# Revit family: TopVent_THC
name_source: partatom
category: Mechanical Equipment
revit_build: Autodesk Revit MEP 2015 (Build: 20160512_0715(x64)
units: mm (PartAtom-declared; Revit-internal decimal feet)

## types (9) — shared parameters
COBIE Connected load = 3.6 kW
COBIE Current consumption max. = 5.9A
COBIE Extract air temperature max. = 50°C
COBIE Frequency = 50 Hz
COBIE Permitted voltage tolerance = +/-5%
COBIE Pressure of the heating medium max. = 800 kPa
COBIE Protection rating = IP 54
COBIE Series fuse = 13A
COBIE Static efficiency of the fans = 63.6%
COBIE Supply air temperature max. = 60°C
COBIE Supply voltage = 3x400 V AC
COBIE Temperature of the heating medium max. = 90°C
Connected load = 3.6 kW
Current consumption max. = 5.9A
Extract air temperature max. = 50°C
Frequency = 50 Hz
Permitted voltage tolerance = +/-5%
Pressure of the heating medium max. = 800 kPa
Protection rating = IP 54
S = 25 mm  [stored 0.082021 ft]
Series fuse = 13A
Static efficiency of the fans = 63.6%
Supply air temperature max. = 60°C
Supply voltage = 3x400 V AC
Temperature of the heating medium max. = 90°C

## per-type parameters (varying)
- THC-6-AC: (X)=1120 mm  [stored 3.67454 ft]; A=900 mm  [stored 2.95276 ft]; Air flow rate=3100 m3/h; B=1647 mm  [stored 5.40354 ft]; COBIE Air flow rate=3100 m3/h; COBIE Condensate quantity=90 kg/h; COBIE Condensate quantity 22 °C (50/70 %) - 6/12 °C=0.0/13.5 kg/h; COBIE Condensate quantity 22 °C (50/70 %) - 8/14 °C=0.0/7.9 kg/h; COBIE Condensate quantity 26 °C (50/70 %) - 6/12 °C=8.6/30.2 kg/h; COBIE Condensate quantity 26 °C (50/70 %) - 8/14 °C=3.0/24.6 kg/h; COBIE Effective electric power input=0.72 kW; COBIE Floor area covered=537.0; COBIE Heat output 16/20 °C (60/40 °C)=18.8/16.2 kW; COBIE Heat output 16/20 °C (80/60 °C)=32.8/30.3 kW; COBIE Maximum mounting height 16/20 °C (60/40 °C)=16.8/17.9 m; COBIE Maximum mounting height 16/20 °C (80/60 °C)=13.4/14.0 m; COBIE Nominal air flow rate=6000.0; COBIE Octave sound power level - 1000 Hz=71 dB; COBIE Octave sound power level - 125 Hz=59 dB; COBIE Octave sound power level - 2000 Hz=71 dB; COBIE Octave sound power level - 250 Hz=62 dB; COBIE Octave sound power level - 4000 Hz=67 dB; COBIE Octave sound power level - 500 Hz=68 dB; COBIE Octave sound power level - 63 Hz=41 dB; COBIE Octave sound power level - 8000 Hz=58 dB; COBIE Sensible cooling capacity 22 °C (50/70 %) - 6/12 °C=20.4/18.5 kW; COBIE Sensible cooling capacity 22 °C (50/70 %) - 8/14 °C=20.4/16.0 kW; COBIE Sensible cooling capacity 26 °C (50/70 %) - 6/12 °C=25.2/23.2 kW; COBIE Sensible cooling capacity 26 °C (50/70 %) - 8/14 °C=22.7/20.8 kW; COBIE Sound pressure level (at a distance of 5 m)=54 dB(A); COBIE Supply air temperature 16/20 °C (60/40 °C)=27.3/30.0 °C; COBIE Supply air temperature 16/20 °C (80/60 °C)=34.2/37.0 °C; COBIE Supply air temperature 22 °C (50/70 %) - 6/12 °C=13.9/14.9 °C; COBIE Supply air temperature 22 °C (50/70 %) - 8/14 °C=13.9/16.1 °C; COBIE Supply air temperature 26 °C (50/70 %) - 6/12 °C=15.5/16.5 °C; COBIE Supply air temperature 26 °C (50/70 %) - 8/14 °C=16.7/17.7 °C; COBIE Total cooling capacity 22 °C (50/70 %) - 6/12 °C=20.4/27.7 kW; COBIE Total cooling capacity 22 °C (50/70 %) - 8/14 °C=20.4/21.4 kW; COBIE Total cooling capacity 26 °C (50/70 %) - 6/12 °C=31.1/43.7 kW; COBIE Total cooling capacity 26 °C (50/70 %) - 8/14 °C=24.8/37.5 kW; COBIE Total sound power level=76 dB(A); COBIE Water content of cooling coil=7.9 l; COBIE Water content of heating coil=4.6 l; COBIE Water pressure drop 16/20 °C (60/40 °C)=2/2 kPa; COBIE Water pressure drop 16/20 °C (80/60 °C)=7/6 kPa; COBIE Water pressure drop 22 °C (50/70 %) - 6/12 °C=15/28 kPa; COBIE Water pressure drop 22 °C (50/70 %) - 8/14 °C=15/17 kPa; COBIE Water pressure drop 26 °C (50/70 %) - 6/12 °C=36/71 kPa; COBIE Water pressure drop 26 °C (50/70 %) - 8/14 °C=23/52 kPa; COBIE Water quantity 16/20 °C (60/40 °C)=807/697 l/h; COBIE Water quantity 16/20 °C (80/60 °C)=1410/1301 l/h; COBIE Water quantity 22 °C (50/70 %) - 6/12 °C=2925/3960 l/h; COBIE Water quantity 22 °C (50/70 %) - 8/14 °C=2925/3064 l/h; COBIE Water quantity 26 °C (50/70 %) - 6/12 °C=4448/6263 l/h; COBIE Water quantity 26 °C (50/70 %) - 8/14 °C=3552/5367 l/h; COBIE Weight=248 kg; Condensate quantity=90 kg/h; Condensate quantity 22 °C (50/70 %) - 6/12 °C=0.0/13.5 kg/h; Condensate quantity 22 °C (50/70 %) - 8/14 °C=0.0/7.9 kg/h; Condensate quantity 26 °C (50/70 %) - 6/12 °C=8.6/30.2 kg/h; Condensate quantity 26 °C (50/70 %) - 8/14 °C=3.0/24.6 kg/h; E=594 mm  [stored 1.94882 ft]; E/2=297 mm  [stored 0.974409 ft]; Effective electric power input=0.72 kW; F=758 mm  [stored 2.48688 ft]; Floor area covered=537 m²; G=101 mm  [stored 0.331365 ft]; H=179 mm  [stored 0.58727 ft]; Heat output 16/20 °C (60/40 °C)=18.8/16.2 kW; Heat output 16/20 °C (80/60 °C)=32.8/30.3 kW; I=349 mm  [stored 1.14501 ft]; J=427 mm  [stored 1.40092 ft]; K=760 mm  [stored 2.49344 ft]; Maximum mounting height 16/20 °C (60/40 °C)=16.8/17.9 m; Maximum mounting height 16/20 °C (80/60 °C)=13.4/14.0 m; N=1030 mm  [stored 3.37927 ft]; Nominal air flow rate=6000 m³/h; O=792 mm  [stored 2.59843 ft]; Octave sound power level - 1000 Hz=71 dB; Octave sound power level - 125 Hz=59 dB; Octave sound power level - 2000 Hz=71 dB; Octave sound power level - 250 Hz=62 dB; Octave sound power level - 4000 Hz=67 dB; Octave sound power level - 500 Hz=68 dB; Octave sound power level - 63 Hz=41 dB; Octave sound power level - 8000 Hz=58 dB; P=312 mm  [stored 1.02362 ft]; Q=32 mm  [stored 0.104987 ft]; R=32 mm  [stored 0.104987 ft]; Sensible cooling capacity 22 °C (50/70 %) - 6/12 °C=20.4/18.5 kW; Sensible cooling capacity 22 °C (50/70 %) - 8/14 °C=20.4/16.0 kW; Sensible cooling capacity 26 °C (50/70 %) - 6/12 °C=25.2/23.2 kW; Sensible cooling capacity 26 °C (50/70 %) - 8/14 °C=22.7/20.8 kW; Sound pressure level (at a distance of 5 m)=54 dB(A); Supply air temperature 16/20 °C (60/40 °C)=27.3/30.0 °C; Supply air temperature 16/20 °C (80/60 °C)=34.2/37.0 °C; Supply air temperature 22 °C (50/70 %) - 6/12 °C=13.9/14.9 °C; Supply air temperature 22 °C (50/70 %) - 8/14 °C=13.9/16.1 °C; Supply air temperature 26 °C (50/70 %) - 6/12 °C=15.5/16.5 °C; Supply air temperature 26 °C (50/70 %) - 8/14 °C=16.7/17.7 °C; Total cooling capacity 22 °C (50/70 %) - 6/12 °C=20.4/27.7 kW; Total cooling capacity 22 °C (50/70 %) - 8/14 °C=20.4/21.4 kW; Total cooling capacity 26 °C (50/70 %) - 6/12 °C=31.1/43.7 kW; Total cooling capacity 26 °C (50/70 %) - 8/14 °C=24.8/37.5 kW; Total sound power level=76 dB(A); Water content of cooling coil=7.9 l; Water content of heating coil=4.6 l; Water pressure drop 16/20 °C (60/40 °C)=2/2 kPa; Water pressure drop 16/20 °C (80/60 °C)=7/6 kPa; Water pressure drop 22 °C (50/70 %) - 6/12 °C=15/28 kPa; Water pressure drop 22 °C (50/70 %) - 8/14 °C=15/17 kPa; Water pressure drop 26 °C (50/70 %) - 6/12 °C=36/71 kPa; Water pressure drop 26 °C (50/70 %) - 8/14 °C=23/52 kPa; Water quantity 16/20 °C (60/40 °C)=807/697 l/h; Water quantity 16/20 °C (80/60 °C)=1410/1301 l/h; Water quantity 22 °C (50/70 %) - 6/12 °C=2925/3960 l/h; Water quantity 22 °C (50/70 %) - 8/14 °C=2925/3064 l/h; Water quantity 26 °C (50/70 %) - 6/12 °C=4448/6263 l/h; Water quantity 26 °C (50/70 %) - 8/14 °C=3552/5367 l/h; Weight=248 kg
- THC-6-BC: (X)=1120 mm  [stored 3.67454 ft]; A=900 mm  [stored 2.95276 ft]; Air flow rate=3100 m3/h; B=1647 mm  [stored 5.40354 ft]; COBIE Air flow rate=3100 m3/h; COBIE Condensate quantity=90 kg/h; COBIE Condensate quantity 22 °C (50/70 %) - 6/12 °C=0.0/13.5 kg/h; COBIE Condensate quantity 22 °C (50/70 %) - 8/14 °C=0.0/7.9 kg/h; COBIE Condensate quantity 26 °C (50/70 %) - 6/12 °C=8.6/30.2 kg/h; COBIE Condensate quantity 26 °C (50/70 %) - 8/14 °C=3.0/24.6 kg/h; COBIE Effective electric power input=0.76 kW; COBIE Floor area covered=537.0; COBIE Heat output 16/20 °C (60/40 °C)=26.9/23.3 kW; COBIE Heat output 16/20 °C (80/60 °C)=47.0/43.4 kW; COBIE Maximum mounting height 16/20 °C (60/40 °C)=14.6/15.5 m; COBIE Maximum mounting height 16/20 °C (80/60 °C)=11.6/12.0 m; COBIE Nominal air flow rate=6000.0; COBIE Octave sound power level - 1000 Hz=71 dB; COBIE Octave sound power level - 125 Hz=59 dB; COBIE Octave sound power level - 2000 Hz=71 dB; COBIE Octave sound power level - 250 Hz=62 dB; COBIE Octave sound power level - 4000 Hz=67 dB; COBIE Octave sound power level - 500 Hz=68 dB; COBIE Octave sound power level - 63 Hz=41 dB; COBIE Octave sound power level - 8000 Hz=58 dB; COBIE Sensible cooling capacity 22 °C (50/70 %) - 6/12 °C=20.4/18.5 kW; COBIE Sensible cooling capacity 22 °C (50/70 %) - 8/14 °C=20.4/16.0 kW; COBIE Sensible cooling capacity 26 °C (50/70 %) - 6/12 °C=25.2/23.2 kW; COBIE Sensible cooling capacity 26 °C (50/70 %) - 8/14 °C=22.7/20.8 kW; COBIE Sound pressure level (at a distance of 5 m)=54 dB(A); COBIE Supply air temperature 16/20 °C (60/40 °C)=31.3/33.5 °C; COBIE Supply air temperature 16/20 °C (80/60 °C)=41.3/43.5 °C; COBIE Supply air temperature 22 °C (50/70 %) - 6/12 °C=13.9/14.9 °C; COBIE Supply air temperature 22 °C (50/70 %) - 8/14 °C=13.9/16.1 °C; COBIE Supply air temperature 26 °C (50/70 %) - 6/12 °C=15.5/16.5 °C; COBIE Supply air temperature 26 °C (50/70 %) - 8/14 °C=16.7/17.7 °C; COBIE Total cooling capacity 22 °C (50/70 %) - 6/12 °C=20.4/27.7 kW; COBIE Total cooling capacity 22 °C (50/70 %) - 8/14 °C=20.4/21.4 kW; COBIE Total cooling capacity 26 °C (50/70 %) - 6/12 °C=31.1/43.7 kW; COBIE Total cooling capacity 26 °C (50/70 %) - 8/14 °C=24.8/37.5 kW; COBIE Total sound power level=76 dB(A); COBIE Water content of cooling coil=7.9 l; COBIE Water content of heating coil=4.6 l; COBIE Water pressure drop 16/20 °C (60/40 °C)=4/3 kPa; COBIE Water pressure drop 16/20 °C (80/60 °C)=13/11 kPa; COBIE Water pressure drop 22 °C (50/70 %) - 6/12 °C=15/28 kPa; COBIE Water pressure drop 22 °C (50/70 %) - 8/14 °C=15/17 kPa; COBIE Water pressure drop 26 °C (50/70 %) - 6/12 °C=36/71 kPa; COBIE Water pressure drop 26 °C (50/70 %) - 8/14 °C=23/52 kPa; COBIE Water quantity 16/20 °C (60/40 °C)=1157/1001 l/h; COBIE Water quantity 16/20 °C (80/60 °C)=2020/1864 l/h; COBIE Water quantity 22 °C (50/70 %) - 6/12 °C=2925/3960 l/h; COBIE Water quantity 22 °C (50/70 %) - 8/14 °C=2925/3064 l/h; COBIE Water quantity 26 °C (50/70 %) - 6/12 °C=4448/6263 l/h; COBIE Water quantity 26 °C (50/70 %) - 8/14 °C=3552/5367 l/h; COBIE Weight=248 kg; Condensate quantity=90 kg/h; Condensate quantity 22 °C (50/70 %) - 6/12 °C=0.0/13.5 kg/h; Condensate quantity 22 °C (50/70 %) - 8/14 °C=0.0/7.9 kg/h; Condensate quantity 26 °C (50/70 %) - 6/12 °C=8.6/30.2 kg/h; Condensate quantity 26 °C (50/70 %) - 8/14 °C=3.0/24.6 kg/h; E=594 mm  [stored 1.94882 ft]; E/2=297 mm  [stored 0.974409 ft]; Effective electric power input=0.76 kW; F=758 mm  [stored 2.48688 ft]; Floor area covered=537 m²; G=101 mm  [stored 0.331365 ft]; H=179 mm  [stored 0.58727 ft]; Heat output 16/20 °C (60/40 °C)=26.9/23.3 kW; Heat output 16/20 °C (80/60 °C)=47.0/43.4 kW; I=349 mm  [stored 1.14501 ft]; J=427 mm  [stored 1.40092 ft]; K=760 mm  [stored 2.49344 ft]; Maximum mounting height 16/20 °C (60/40 °C)=14.6/15.5 m; Maximum mounting height 16/20 °C (80/60 °C)=11.6/12.0 m; N=1030 mm  [stored 3.37927 ft]; Nominal air flow rate=6000 m³/h; O=792 mm  [stored 2.59843 ft]; Octave sound power level - 1000 Hz=71 dB; Octave sound power level - 125 Hz=59 dB; Octave sound power level - 2000 Hz=71 dB; Octave sound power level - 250 Hz=62 dB; Octave sound power level - 4000 Hz=67 dB; Octave sound power level - 500 Hz=68 dB; Octave sound power level - 63 Hz=41 dB; Octave sound power level - 8000 Hz=58 dB; P=312 mm  [stored 1.02362 ft]; Q=32 mm  [stored 0.104987 ft]; R=32 mm  [stored 0.104987 ft]; Sensible cooling capacity 22 °C (50/70 %) - 6/12 °C=20.4/18.5 kW; Sensible cooling capacity 22 °C (50/70 %) - 8/14 °C=20.4/16.0 kW; Sensible cooling capacity 26 °C (50/70 %) - 6/12 °C=25.2/23.2 kW; Sensible cooling capacity 26 °C (50/70 %) - 8/14 °C=22.7/20.8 kW; Sound pressure level (at a distance of 5 m)=54 dB(A); Supply air temperature 16/20 °C (60/40 °C)=31.3/33.5 °C; Supply air temperature 16/20 °C (80/60 °C)=41.3/43.5 °C; Supply air temperature 22 °C (50/70 %) - 6/12 °C=13.9/14.9 °C; Supply air temperature 22 °C (50/70 %) - 8/14 °C=13.9/16.1 °C; Supply air temperature 26 °C (50/70 %) - 6/12 °C=15.5/16.5 °C; Supply air temperature 26 °C (50/70 %) - 8/14 °C=16.7/17.7 °C; Total cooling capacity 22 °C (50/70 %) - 6/12 °C=20.4/27.7 kW; Total cooling capacity 22 °C (50/70 %) - 8/14 °C=20.4/21.4 kW; Total cooling capacity 26 °C (50/70 %) - 6/12 °C=31.1/43.7 kW; Total cooling capacity 26 °C (50/70 %) - 8/14 °C=24.8/37.5 kW; Total sound power level=76 dB(A); Water content of cooling coil=7.9 l; Water content of heating coil=4.6 l; Water pressure drop 16/20 °C (60/40 °C)=4/3 kPa; Water pressure drop 16/20 °C (80/60 °C)=13/11 kPa; Water pressure drop 22 °C (50/70 %) - 6/12 °C=15/28 kPa; Water pressure drop 22 °C (50/70 %) - 8/14 °C=15/17 kPa; Water pressure drop 26 °C (50/70 %) - 6/12 °C=36/71 kPa; Water pressure drop 26 °C (50/70 %) - 8/14 °C=23/52 kPa; Water quantity 16/20 °C (60/40 °C)=1157/1001 l/h; Water quantity 16/20 °C (80/60 °C)=2020/1864 l/h; Water quantity 22 °C (50/70 %) - 6/12 °C=2925/3960 l/h; Water quantity 22 °C (50/70 %) - 8/14 °C=2925/3064 l/h; Water quantity 26 °C (50/70 %) - 6/12 °C=4448/6263 l/h; Water quantity 26 °C (50/70 %) - 8/14 °C=3552/5367 l/h; Weight=248 kg
- THC-6-CC: (X)=1120 mm  [stored 3.67454 ft]; A=900 mm  [stored 2.95276 ft]; Air flow rate=3100 m3/h; B=1647 mm  [stored 5.40354 ft]; COBIE Air flow rate=3100 m3/h; COBIE Condensate quantity=90 kg/h; COBIE Condensate quantity 22 °C (50/70 %) - 6/12 °C=0.0/13.5 kg/h; COBIE Condensate quantity 22 °C (50/70 %) - 8/14 °C=0.0/7.9 kg/h; COBIE Condensate quantity 26 °C (50/70 %) - 6/12 °C=8.6/30.2 kg/h; COBIE Condensate quantity 26 °C (50/70 %) - 8/14 °C=3.0/24.6 kg/h; COBIE Effective electric power input=0.87 kW; COBIE Floor area covered=537.0; COBIE Heat output 16/20 °C (60/40 °C)=45.0/39.3 kW; COBIE Heat output 16/20 °C (80/60 °C)=76.0/70.3 kW; COBIE Maximum mounting height 16/20 °C (60/40 °C)=11.8/12.5 m; COBIE Maximum mounting height 16/20 °C (80/60 °C)=9.4/9.8 m; COBIE Nominal air flow rate=6000.0; COBIE Octave sound power level - 1000 Hz=71 dB; COBIE Octave sound power level - 125 Hz=59 dB; COBIE Octave sound power level - 2000 Hz=71 dB; COBIE Octave sound power level - 250 Hz=62 dB; COBIE Octave sound power level - 4000 Hz=67 dB; COBIE Octave sound power level - 500 Hz=68 dB; COBIE Octave sound power level - 63 Hz=41 dB; COBIE Octave sound power level - 8000 Hz=58 dB; COBIE Sensible cooling capacity 22 °C (50/70 %) - 6/12 °C=20.4/18.5 kW; COBIE Sensible cooling capacity 22 °C (50/70 %) - 8/14 °C=20.4/16.0 kW; COBIE Sensible cooling capacity 26 °C (50/70 %) - 6/12 °C=25.2/23.2 kW; COBIE Sensible cooling capacity 26 °C (50/70 %) - 8/14 °C=22.7/20.8 kW; COBIE Sound pressure level (at a distance of 5 m)=54 dB(A); COBIE Supply air temperature 16/20 °C (60/40 °C)=40.3/41.5 °C; COBIE Supply air temperature 16/20 °C (80/60 °C)=55.6/56.8 °C; COBIE Supply air temperature 22 °C (50/70 %) - 6/12 °C=13.9/14.9 °C; COBIE Supply air temperature 22 °C (50/70 %) - 8/14 °C=13.9/16.1 °C; COBIE Supply air temperature 26 °C (50/70 %) - 6/12 °C=15.5/16.5 °C; COBIE Supply air temperature 26 °C (50/70 %) - 8/14 °C=16.7/17.7 °C; COBIE Total cooling capacity 22 °C (50/70 %) - 6/12 °C=20.4/27.7 kW; COBIE Total cooling capacity 22 °C (50/70 %) - 8/14 °C=20.4/21.4 kW; COBIE Total cooling capacity 26 °C (50/70 %) - 6/12 °C=31.1/43.7 kW; COBIE Total cooling capacity 26 °C (50/70 %) - 8/14 °C=24.8/37.5 kW; COBIE Total sound power level=76 dB(A); COBIE Water content of cooling coil=7.9 l; COBIE Water content of heating coil=7.9 l; COBIE Water pressure drop 16/20 °C (60/40 °C)=6/5 kPa; COBIE Water pressure drop 16/20 °C (80/60 °C)=18/16 kPa; COBIE Water pressure drop 22 °C (50/70 %) - 6/12 °C=15/28 kPa; COBIE Water pressure drop 22 °C (50/70 %) - 8/14 °C=15/17 kPa; COBIE Water pressure drop 26 °C (50/70 %) - 6/12 °C=36/71 kPa; COBIE Water pressure drop 26 °C (50/70 %) - 8/14 °C=23/52 kPa; COBIE Water quantity 16/20 °C (60/40 °C)=1935/1690 l/h; COBIE Water quantity 16/20 °C (80/60 °C)=3267/3022 l/h; COBIE Water quantity 22 °C (50/70 %) - 6/12 °C=2925/3960 l/h; COBIE Water quantity 22 °C (50/70 %) - 8/14 °C=2925/3064 l/h; COBIE Water quantity 26 °C (50/70 %) - 6/12 °C=4448/6263 l/h; COBIE Water quantity 26 °C (50/70 %) - 8/14 °C=3552/5367 l/h; COBIE Weight=255 kg; Condensate quantity=90 kg/h; Condensate quantity 22 °C (50/70 %) - 6/12 °C=0.0/13.5 kg/h; Condensate quantity 22 °C (50/70 %) - 8/14 °C=0.0/7.9 kg/h; Condensate quantity 26 °C (50/70 %) - 6/12 °C=8.6/30.2 kg/h; Condensate quantity 26 °C (50/70 %) - 8/14 °C=3.0/24.6 kg/h; E=594 mm  [stored 1.94882 ft]; E/2=297 mm  [stored 0.974409 ft]; Effective electric power input=0.87 kW; F=758 mm  [stored 2.48688 ft]; Floor area covered=537 m²; G=101 mm  [stored 0.331365 ft]; H=179 mm  [stored 0.58727 ft]; Heat output 16/20 °C (60/40 °C)=45.0/39.3 kW; Heat output 16/20 °C (80/60 °C)=76.0/70.3 kW; I=349 mm  [stored 1.14501 ft]; J=427 mm  [stored 1.40092 ft]; K=760 mm  [stored 2.49344 ft]; Maximum mounting height 16/20 °C (60/40 °C)=11.8/12.5 m; Maximum mounting height 16/20 °C (80/60 °C)=9.4/9.8 m; N=1030 mm  [stored 3.37927 ft]; Nominal air flow rate=6000 m³/h; O=792 mm  [stored 2.59843 ft]; Octave sound power level - 1000 Hz=71 dB; Octave sound power level - 125 Hz=59 dB; Octave sound power level - 2000 Hz=71 dB; Octave sound power level - 250 Hz=62 dB; Octave sound power level - 4000 Hz=67 dB; Octave sound power level - 500 Hz=68 dB; Octave sound power level - 63 Hz=41 dB; Octave sound power level - 8000 Hz=58 dB; P=312 mm  [stored 1.02362 ft]; Q=32 mm  [stored 0.104987 ft]; R=32 mm  [stored 0.104987 ft]; Sensible cooling capacity 22 °C (50/70 %) - 6/12 °C=20.4/18.5 kW; Sensible cooling capacity 22 °C (50/70 %) - 8/14 °C=20.4/16.0 kW; Sensible cooling capacity 26 °C (50/70 %) - 6/12 °C=25.2/23.2 kW; Sensible cooling capacity 26 °C (50/70 %) - 8/14 °C=22.7/20.8 kW; Sound pressure level (at a distance of 5 m)=54 dB(A); Supply air temperature 16/20 °C (60/40 °C)=40.3/41.5 °C; Supply air temperature 16/20 °C (80/60 °C)=55.6/56.8 °C; Supply air temperature 22 °C (50/70 %) - 6/12 °C=13.9/14.9 °C; Supply air temperature 22 °C (50/70 %) - 8/14 °C=13.9/16.1 °C; Supply air temperature 26 °C (50/70 %) - 6/12 °C=15.5/16.5 °C; Supply air temperature 26 °C (50/70 %) - 8/14 °C=16.7/17.7 °C; Total cooling capacity 22 °C (50/70 %) - 6/12 °C=20.4/27.7 kW; Total cooling capacity 22 °C (50/70 %) - 8/14 °C=20.4/21.4 kW; Total cooling capacity 26 °C (50/70 %) - 6/12 °C=31.1/43.7 kW; Total cooling capacity 26 °C (50/70 %) - 8/14 °C=24.8/37.5 kW; Total sound power level=76 dB(A); Water content of cooling coil=7.9 l; Water content of heating coil=7.9 l; Water pressure drop 16/20 °C (60/40 °C)=6/5 kPa; Water pressure drop 16/20 °C (80/60 °C)=18/16 kPa; Water pressure drop 22 °C (50/70 %) - 6/12 °C=15/28 kPa; Water pressure drop 22 °C (50/70 %) - 8/14 °C=15/17 kPa; Water pressure drop 26 °C (50/70 %) - 6/12 °C=36/71 kPa; Water pressure drop 26 °C (50/70 %) - 8/14 °C=23/52 kPa; Water quantity 16/20 °C (60/40 °C)=1935/1690 l/h; Water quantity 16/20 °C (80/60 °C)=3267/3022 l/h; Water quantity 22 °C (50/70 %) - 6/12 °C=2925/3960 l/h; Water quantity 22 °C (50/70 %) - 8/14 °C=2925/3064 l/h; Water quantity 26 °C (50/70 %) - 6/12 °C=4448/6263 l/h; Water quantity 26 °C (50/70 %) - 8/14 °C=3552/5367 l/h; Weight=255 kg
- THC-9-AC: (X)=1238 mm  [stored 4.06168 ft]; A=1100 mm; Air flow rate=5000 m3/h; B=1765 mm  [stored 5.79068 ft]; COBIE Air flow rate=5000 m3/h; COBIE Condensate quantity=150 kg/h; COBIE Condensate quantity 22 °C (50/70 %) - 6/12 °C=0.0/23.9 kg/h; COBIE Condensate quantity 22 °C (50/70 %) - 8/14 °C=0.0/5.2 kg/h; COBIE Condensate quantity 26 °C (50/70 %) - 6/12 °C=16.3/49.8 kg/h; COBIE Condensate quantity 26 °C (50/70 %) - 8/14 °C=0.0/31.1 kg/h; COBIE Effective electric power input=1.37 kW; COBIE Floor area covered=946.0; COBIE Heat output 16/20 °C (60/40 °C)=31.7/27.4 kW; COBIE Heat output 16/20 °C (80/60 °C)=55.5/51.2 kW; COBIE Maximum mounting height 16/20 °C (60/40 °C)=17.0/18.1 m; COBIE Maximum mounting height 16/20 °C (80/60 °C)=13.6/14.1 m; COBIE Nominal air flow rate=9000.0; COBIE Octave sound power level - 1000 Hz=77 dB; COBIE Octave sound power level - 125 Hz=66 dB; COBIE Octave sound power level - 2000 Hz=76 dB; COBIE Octave sound power level - 250 Hz=69 dB; COBIE Octave sound power level - 4000 Hz=74 dB; COBIE Octave sound power level - 500 Hz=74 dB; COBIE Octave sound power level - 63 Hz=47 dB; COBIE Octave sound power level - 8000 Hz=67 dB; COBIE Sensible cooling capacity 22 °C (50/70 %) - 6/12 °C=31.4/28.4 kW; COBIE Sensible cooling capacity 22 °C (50/70 %) - 8/14 °C=31.4/24.6 kW; COBIE Sensible cooling capacity 26 °C (50/70 %) - 6/12 °C=38.8/35.9 kW; COBIE Sensible cooling capacity 26 °C (50/70 %) - 8/14 °C=35.0/32.0 kW; COBIE Sound pressure level (at a distance of 5 m)=60 dB(A); COBIE Supply air temperature 16/20 °C (60/40 °C)=28.5/31.1 °C; COBIE Supply air temperature 16/20 °C (80/60 °C)=36.3/38.9 °C; COBIE Supply air temperature 22 °C (50/70 %) - 6/12 °C=13.6/14.6 °C; COBIE Supply air temperature 22 °C (50/70 %) - 8/14 °C=13.6/15.9 °C; COBIE Supply air temperature 26 °C (50/70 %) - 6/12 °C=15.2/16.2 °C; COBIE Supply air temperature 26 °C (50/70 %) - 8/14 °C=16.4/17.4 °C; COBIE Total cooling capacity 22 °C (50/70 %) - 6/12 °C=31.4/44.7 kW; COBIE Total cooling capacity 22 °C (50/70 %) - 8/14 °C=31.4/28.2 kW; COBIE Total cooling capacity 26 °C (50/70 %) - 6/12 °C=49.9/69.8 kW; COBIE Total cooling capacity 26 °C (50/70 %) - 8/14 °C=35.0/53.2 kW; COBIE Total sound power level=82 dB(A); COBIE Water content of cooling coil=12.4 l; COBIE Water content of heating coil=7.4 l; COBIE Water pressure drop 16/20 °C (60/40 °C)=3/2 kPa; COBIE Water pressure drop 16/20 °C (80/60 °C)=8/7 kPa; COBIE Water pressure drop 22 °C (50/70 %) - 6/12 °C=15/31 kPa; COBIE Water pressure drop 22 °C (50/70 %) - 8/14 °C=15/12 kPa; COBIE Water pressure drop 26 °C (50/70 %) - 6/12 °C=38/75 kPa; COBIE Water pressure drop 26 °C (50/70 %) - 8/14 °C=19/44 kPa; COBIE Water quantity 16/20 °C (60/40 °C)=1364/1179 l/h; COBIE Water quantity 16/20 °C (80/60 °C)=2386/2201 l/h; COBIE Water quantity 22 °C (50/70 %) - 6/12 °C=4496/6401 l/h; COBIE Water quantity 22 °C (50/70 %) - 8/14 °C=4496/4031 l/h; COBIE Water quantity 26 °C (50/70 %) - 6/12 °C=7149/9989 l/h; COBIE Water quantity 26 °C (50/70 %) - 8/14 °C=5013/7619 l/h; COBIE Weight=318 kg; Condensate quantity=150 kg/h; Condensate quantity 22 °C (50/70 %) - 6/12 °C=0.0/23.9 kg/h; Condensate quantity 22 °C (50/70 %) - 8/14 °C=0.0/5.2 kg/h; Condensate quantity 26 °C (50/70 %) - 6/12 °C=16.3/49.8 kg/h; Condensate quantity 26 °C (50/70 %) - 8/14 °C=0.0/31.1 kg/h; E=846 mm  [stored 2.77559 ft]; E/2=423 mm  [stored 1.3878 ft]; Effective electric power input=1.37 kW; F=882 mm  [stored 2.8937 ft]; Floor area covered=946 m²; G=111 mm; H=189 mm  [stored 0.620079 ft]; Heat output 16/20 °C (60/40 °C)=31.7/27.4 kW; Heat output 16/20 °C (80/60 °C)=55.5/51.2 kW; I=395 mm  [stored 1.29593 ft]; J=473 mm  [stored 1.55184 ft]; K=935 mm; Maximum mounting height 16/20 °C (60/40 °C)=17.0/18.1 m; Maximum mounting height 16/20 °C (80/60 °C)=13.6/14.1 m; N=1230 mm  [stored 4.03543 ft]; Nominal air flow rate=9000 m³/h; O=860 mm; Octave sound power level - 1000 Hz=77 dB; Octave sound power level - 125 Hz=66 dB; Octave sound power level - 2000 Hz=76 dB; Octave sound power level - 250 Hz=69 dB; Octave sound power level - 4000 Hz=74 dB; Octave sound power level - 500 Hz=74 dB; Octave sound power level - 63 Hz=47 dB; Octave sound power level - 8000 Hz=67 dB; P=342 mm  [stored 1.12205 ft]; Q=38 mm; R=38 mm; Sensible cooling capacity 22 °C (50/70 %) - 6/12 °C=31.4/28.4 kW; Sensible cooling capacity 22 °C (50/70 %) - 8/14 °C=31.4/24.6 kW; Sensible cooling capacity 26 °C (50/70 %) - 6/12 °C=38.8/35.9 kW; Sensible cooling capacity 26 °C (50/70 %) - 8/14 °C=35.0/32.0 kW; Sound pressure level (at a distance of 5 m)=60 dB(A); Supply air temperature 16/20 °C (60/40 °C)=28.5/31.1 °C; Supply air temperature 16/20 °C (80/60 °C)=36.3/38.9 °C; Supply air temperature 22 °C (50/70 %) - 6/12 °C=13.6/14.6 °C; Supply air temperature 22 °C (50/70 %) - 8/14 °C=13.6/15.9 °C; Supply air temperature 26 °C (50/70 %) - 6/12 °C=15.2/16.2 °C; Supply air temperature 26 °C (50/70 %) - 8/14 °C=16.4/17.4 °C; Total cooling capacity 22 °C (50/70 %) - 6/12 °C=31.4/44.7 kW; Total cooling capacity 22 °C (50/70 %) - 8/14 °C=31.4/28.2 kW; Total cooling capacity 26 °C (50/70 %) - 6/12 °C=49.9/69.8 kW; Total cooling capacity 26 °C (50/70 %) - 8/14 °C=35.0/53.2 kW; Total sound power level=82 dB(A); Water content of cooling coil=12.4 l; Water content of heating coil=7.4 l; Water pressure drop 16/20 °C (60/40 °C)=3/2 kPa; Water pressure drop 16/20 °C (80/60 °C)=8/7 kPa; Water pressure drop 22 °C (50/70 %) - 6/12 °C=15/31 kPa; Water pressure drop 22 °C (50/70 %) - 8/14 °C=15/12 kPa; Water pressure drop 26 °C (50/70 %) - 6/12 °C=38/75 kPa; Water pressure drop 26 °C (50/70 %) - 8/14 °C=19/44 kPa; Water quantity 16/20 °C (60/40 °C)=1364/1179 l/h; Water quantity 16/20 °C (80/60 °C)=2386/2201 l/h; Water quantity 22 °C (50/70 %) - 6/12 °C=4496/6401 l/h; Water quantity 22 °C (50/70 %) - 8/14 °C=4496/4031 l/h; Water quantity 26 °C (50/70 %) - 6/12 °C=7149/9989 l/h; Water quantity 26 °C (50/70 %) - 8/14 °C=5013/7619 l/h; Weight=318 kg
- THC-9-BC: (X)=1238 mm  [stored 4.06168 ft]; A=1100 mm; Air flow rate=5000 m3/h; B=1765 mm  [stored 5.79068 ft]; COBIE Air flow rate=5000 m3/h; COBIE Condensate quantity=150 kg/h; COBIE Condensate quantity 22 °C (50/70 %) - 6/12 °C=0.0/23.9 kg/h; COBIE Condensate quantity 22 °C (50/70 %) - 8/14 °C=0.0/5.2 kg/h; COBIE Condensate quantity 26 °C (50/70 %) - 6/12 °C=16.3/49.8 kg/h; COBIE Condensate quantity 26 °C (50/70 %) - 8/14 °C=0.0/31.1 kg/h; COBIE Effective electric power input=1.49 kW; COBIE Floor area covered=946.0; COBIE Heat output 16/20 °C (60/40 °C)=40.6/35.1 kW; COBIE Heat output 16/20 °C (80/60 °C)=71.2/65.7 kW; COBIE Maximum mounting height 16/20 °C (60/40 °C)=15.4/16.5 m; COBIE Maximum mounting height 16/20 °C (80/60 °C)=12.2/12.7 m; COBIE Nominal air flow rate=9000.0; COBIE Octave sound power level - 1000 Hz=77 dB; COBIE Octave sound power level - 125 Hz=66 dB; COBIE Octave sound power level - 2000 Hz=76 dB; COBIE Octave sound power level - 250 Hz=69 dB; COBIE Octave sound power level - 4000 Hz=74 dB; COBIE Octave sound power level - 500 Hz=74 dB; COBIE Octave sound power level - 63 Hz=47 dB; COBIE Octave sound power level - 8000 Hz=67 dB; COBIE Sensible cooling capacity 22 °C (50/70 %) - 6/12 °C=31.4/28.4 kW; COBIE Sensible cooling capacity 22 °C (50/70 %) - 8/14 °C=31.4/24.6 kW; COBIE Sensible cooling capacity 26 °C (50/70 %) - 6/12 °C=38.8/35.9 kW; COBIE Sensible cooling capacity 26 °C (50/70 %) - 8/14 °C=35.0/32.0 kW; COBIE Sound pressure level (at a distance of 5 m)=60 dB(A); COBIE Supply air temperature 16/20 °C (60/40 °C)=31.4/33.6 °C; COBIE Supply air temperature 16/20 °C (80/60 °C)=41.5/43.7 °C; COBIE Supply air temperature 22 °C (50/70 %) - 6/12 °C=13.6/14.6 °C; COBIE Supply air temperature 22 °C (50/70 %) - 8/14 °C=13.6/15.9 °C; COBIE Supply air temperature 26 °C (50/70 %) - 6/12 °C=15.2/16.2 °C; COBIE Supply air temperature 26 °C (50/70 %) - 8/14 °C=16.4/17.4 °C; COBIE Total cooling capacity 22 °C (50/70 %) - 6/12 °C=31.4/44.7 kW; COBIE Total cooling capacity 22 °C (50/70 %) - 8/14 °C=31.4/28.2 kW; COBIE Total cooling capacity 26 °C (50/70 %) - 6/12 °C=49.9/69.8 kW; COBIE Total cooling capacity 26 °C (50/70 %) - 8/14 °C=35.0/53.2 kW; COBIE Total sound power level=82 dB(A); COBIE Water content of cooling coil=12.4 l; COBIE Water content of heating coil=7.4 l; COBIE Water pressure drop 16/20 °C (60/40 °C)=4/3 kPa; COBIE Water pressure drop 16/20 °C (80/60 °C)=12/10 kPa; COBIE Water pressure drop 22 °C (50/70 %) - 6/12 °C=15/31 kPa; COBIE Water pressure drop 22 °C (50/70 %) - 8/14 °C=15/12 kPa; COBIE Water pressure drop 26 °C (50/70 %) - 6/12 °C=38/75 kPa; COBIE Water pressure drop 26 °C (50/70 %) - 8/14 °C=19/44 kPa; COBIE Water quantity 16/20 °C (60/40 °C)=1746/1509 l/h; COBIE Water quantity 16/20 °C (80/60 °C)=3060/2823 l/h; COBIE Water quantity 22 °C (50/70 %) - 6/12 °C=4496/6401 l/h; COBIE Water quantity 22 °C (50/70 %) - 8/14 °C=4496/4031 l/h; COBIE Water quantity 26 °C (50/70 %) - 6/12 °C=7149/9989 l/h; COBIE Water quantity 26 °C (50/70 %) - 8/14 °C=5013/7619 l/h; COBIE Weight=318 kg; Condensate quantity=150 kg/h; Condensate quantity 22 °C (50/70 %) - 6/12 °C=0.0/23.9 kg/h; Condensate quantity 22 °C (50/70 %) - 8/14 °C=0.0/5.2 kg/h; Condensate quantity 26 °C (50/70 %) - 6/12 °C=16.3/49.8 kg/h; Condensate quantity 26 °C (50/70 %) - 8/14 °C=0.0/31.1 kg/h; E=846 mm  [stored 2.77559 ft]; E/2=423 mm  [stored 1.3878 ft]; Effective electric power input=1.49 kW; F=882 mm  [stored 2.8937 ft]; Floor area covered=946 m²; G=111 mm; H=189 mm  [stored 0.620079 ft]; Heat output 16/20 °C (60/40 °C)=40.6/35.1 kW; Heat output 16/20 °C (80/60 °C)=71.2/65.7 kW; I=395 mm  [stored 1.29593 ft]; J=473 mm  [stored 1.55184 ft]; K=935 mm; Maximum mounting height 16/20 °C (60/40 °C)=15.4/16.5 m; Maximum mounting height 16/20 °C (80/60 °C)=12.2/12.7 m; N=1230 mm  [stored 4.03543 ft]; Nominal air flow rate=9000 m³/h; O=860 mm; Octave sound power level - 1000 Hz=77 dB; Octave sound power level - 125 Hz=66 dB; Octave sound power level - 2000 Hz=76 dB; Octave sound power level - 250 Hz=69 dB; Octave sound power level - 4000 Hz=74 dB; Octave sound power level - 500 Hz=74 dB; Octave sound power level - 63 Hz=47 dB; Octave sound power level - 8000 Hz=67 dB; P=342 mm  [stored 1.12205 ft]; Q=38 mm; R=38 mm; Sensible cooling capacity 22 °C (50/70 %) - 6/12 °C=31.4/28.4 kW; Sensible cooling capacity 22 °C (50/70 %) - 8/14 °C=31.4/24.6 kW; Sensible cooling capacity 26 °C (50/70 %) - 6/12 °C=38.8/35.9 kW; Sensible cooling capacity 26 °C (50/70 %) - 8/14 °C=35.0/32.0 kW; Sound pressure level (at a distance of 5 m)=60 dB(A); Supply air temperature 16/20 °C (60/40 °C)=31.4/33.6 °C; Supply air temperature 16/20 °C (80/60 °C)=41.5/43.7 °C; Supply air temperature 22 °C (50/70 %) - 6/12 °C=13.6/14.6 °C; Supply air temperature 22 °C (50/70 %) - 8/14 °C=13.6/15.9 °C; Supply air temperature 26 °C (50/70 %) - 6/12 °C=15.2/16.2 °C; Supply air temperature 26 °C (50/70 %) - 8/14 °C=16.4/17.4 °C; Total cooling capacity 22 °C (50/70 %) - 6/12 °C=31.4/44.7 kW; Total cooling capacity 22 °C (50/70 %) - 8/14 °C=31.4/28.2 kW; Total cooling capacity 26 °C (50/70 %) - 6/12 °C=49.9/69.8 kW; Total cooling capacity 26 °C (50/70 %) - 8/14 °C=35.0/53.2 kW; Total sound power level=82 dB(A); Water content of cooling coil=12.4 l; Water content of heating coil=7.4 l; Water pressure drop 16/20 °C (60/40 °C)=4/3 kPa; Water pressure drop 16/20 °C (80/60 °C)=12/10 kPa; Water pressure drop 22 °C (50/70 %) - 6/12 °C=15/31 kPa; Water pressure drop 22 °C (50/70 %) - 8/14 °C=15/12 kPa; Water pressure drop 26 °C (50/70 %) - 6/12 °C=38/75 kPa; Water pressure drop 26 °C (50/70 %) - 8/14 °C=19/44 kPa; Water quantity 16/20 °C (60/40 °C)=1746/1509 l/h; Water quantity 16/20 °C (80/60 °C)=3060/2823 l/h; Water quantity 22 °C (50/70 %) - 6/12 °C=4496/6401 l/h; Water quantity 22 °C (50/70 %) - 8/14 °C=4496/4031 l/h; Water quantity 26 °C (50/70 %) - 6/12 °C=7149/9989 l/h; Water quantity 26 °C (50/70 %) - 8/14 °C=5013/7619 l/h; Weight=318 kg
- THC-9-CC: (X)=1238 mm  [stored 4.06168 ft]; A=1100 mm; Air flow rate=5000 m3/h; B=1765 mm  [stored 5.79068 ft]; COBIE Air flow rate=5000 m3/h; COBIE Condensate quantity=150 kg/h; COBIE Condensate quantity 22 °C (50/70 %) - 6/12 °C=0.0/23.9 kg/h; COBIE Condensate quantity 22 °C (50/70 %) - 8/14 °C=0.0/5.2 kg/h; COBIE Condensate quantity 26 °C (50/70 %) - 6/12 °C=16.3/49.8 kg/h; COBIE Condensate quantity 26 °C (50/70 %) - 8/14 °C=0.0/31.1 kg/h; COBIE Effective electric power input=1.42 kW; COBIE Floor area covered=946.0; COBIE Heat output 16/20 °C (60/40 °C)=69.9/61.0 kW; COBIE Heat output 16/20 °C (80/60 °C)=117.9/109.1 kW; COBIE Maximum mounting height 16/20 °C (60/40 °C)=12.3/13.1 m; COBIE Maximum mounting height 16/20 °C (80/60 °C)=9.8/10.2 m; COBIE Nominal air flow rate=9000.0; COBIE Octave sound power level - 1000 Hz=77 dB; COBIE Octave sound power level - 125 Hz=66 dB; COBIE Octave sound power level - 2000 Hz=76 dB; COBIE Octave sound power level - 250 Hz=69 dB; COBIE Octave sound power level - 4000 Hz=74 dB; COBIE Octave sound power level - 500 Hz=74 dB; COBIE Octave sound power level - 63 Hz=47 dB; COBIE Octave sound power level - 8000 Hz=67 dB; COBIE Sensible cooling capacity 22 °C (50/70 %) - 6/12 °C=31.4/28.4 kW; COBIE Sensible cooling capacity 22 °C (50/70 %) - 8/14 °C=31.4/24.6 kW; COBIE Sensible cooling capacity 26 °C (50/70 %) - 6/12 °C=38.8/35.9 kW; COBIE Sensible cooling capacity 26 °C (50/70 %) - 8/14 °C=35.0/32.0 kW; COBIE Sound pressure level (at a distance of 5 m)=60 dB(A); COBIE Supply air temperature 16/20 °C (60/40 °C)=41.1/42.1 °C; COBIE Supply air temperature 16/20 °C (80/60 °C)=56.9/58.0 °C; COBIE Supply air temperature 22 °C (50/70 %) - 6/12 °C=13.6/14.6 °C; COBIE Supply air temperature 22 °C (50/70 %) - 8/14 °C=13.6/15.9 °C; COBIE Supply air temperature 26 °C (50/70 %) - 6/12 °C=15.2/16.2 °C; COBIE Supply air temperature 26 °C (50/70 %) - 8/14 °C=16.4/17.4 °C; COBIE Total cooling capacity 22 °C (50/70 %) - 6/12 °C=31.4/44.7 kW; COBIE Total cooling capacity 22 °C (50/70 %) - 8/14 °C=31.4/28.2 kW; COBIE Total cooling capacity 26 °C (50/70 %) - 6/12 °C=49.9/69.8 kW; COBIE Total cooling capacity 26 °C (50/70 %) - 8/14 °C=35.0/53.2 kW; COBIE Total sound power level=82 dB(A); COBIE Water content of cooling coil=12.4 l; COBIE Water content of heating coil=12.4 l; COBIE Water pressure drop 16/20 °C (60/40 °C)=6/5 kPa; COBIE Water pressure drop 16/20 °C (80/60 °C)=18/15 kPa; COBIE Water pressure drop 22 °C (50/70 %) - 6/12 °C=15/31 kPa; COBIE Water pressure drop 22 °C (50/70 %) - 8/14 °C=15/12 kPa; COBIE Water pressure drop 26 °C (50/70 %) - 6/12 °C=38/75 kPa; COBIE Water pressure drop 26 °C (50/70 %) - 8/14 °C=19/44 kPa; COBIE Water quantity 16/20 °C (60/40 °C)=3003/2622 l/h; COBIE Water quantity 16/20 °C (80/60 °C)=5066/4686 l/h; COBIE Water quantity 22 °C (50/70 %) - 6/12 °C=4496/6401 l/h; COBIE Water quantity 22 °C (50/70 %) - 8/14 °C=4496/4031 l/h; COBIE Water quantity 26 °C (50/70 %) - 6/12 °C=7149/9989 l/h; COBIE Water quantity 26 °C (50/70 %) - 8/14 °C=5013/7619 l/h; COBIE Weight=329 kg; Condensate quantity=150 kg/h; Condensate quantity 22 °C (50/70 %) - 6/12 °C=0.0/23.9 kg/h; Condensate quantity 22 °C (50/70 %) - 8/14 °C=0.0/5.2 kg/h; Condensate quantity 26 °C (50/70 %) - 6/12 °C=16.3/49.8 kg/h; Condensate quantity 26 °C (50/70 %) - 8/14 °C=0.0/31.1 kg/h; E=846 mm  [stored 2.77559 ft]; E/2=423 mm  [stored 1.3878 ft]; Effective electric power input=1.42 kW; F=882 mm  [stored 2.8937 ft]; Floor area covered=946 m²; G=111 mm; H=189 mm  [stored 0.620079 ft]; Heat output 16/20 °C (60/40 °C)=69.9/61.0 kW; Heat output 16/20 °C (80/60 °C)=117.9/109.1 kW; I=395 mm  [stored 1.29593 ft]; J=473 mm  [stored 1.55184 ft]; K=935 mm; Maximum mounting height 16/20 °C (60/40 °C)=12.3/13.1 m; Maximum mounting height 16/20 °C (80/60 °C)=9.8/10.2 m; N=1230 mm  [stored 4.03543 ft]; Nominal air flow rate=9000 m³/h; O=860 mm; Octave sound power level - 1000 Hz=77 dB; Octave sound power level - 125 Hz=66 dB; Octave sound power level - 2000 Hz=76 dB; Octave sound power level - 250 Hz=69 dB; Octave sound power level - 4000 Hz=74 dB; Octave sound power level - 500 Hz=74 dB; Octave sound power level - 63 Hz=47 dB; Octave sound power level - 8000 Hz=67 dB; P=342 mm  [stored 1.12205 ft]; Q=38 mm; R=38 mm; Sensible cooling capacity 22 °C (50/70 %) - 6/12 °C=31.4/28.4 kW; Sensible cooling capacity 22 °C (50/70 %) - 8/14 °C=31.4/24.6 kW; Sensible cooling capacity 26 °C (50/70 %) - 6/12 °C=38.8/35.9 kW; Sensible cooling capacity 26 °C (50/70 %) - 8/14 °C=35.0/32.0 kW; Sound pressure level (at a distance of 5 m)=60 dB(A); Supply air temperature 16/20 °C (60/40 °C)=41.1/42.1 °C; Supply air temperature 16/20 °C (80/60 °C)=56.9/58.0 °C; Supply air temperature 22 °C (50/70 %) - 6/12 °C=13.6/14.6 °C; Supply air temperature 22 °C (50/70 %) - 8/14 °C=13.6/15.9 °C; Supply air temperature 26 °C (50/70 %) - 6/12 °C=15.2/16.2 °C; Supply air temperature 26 °C (50/70 %) - 8/14 °C=16.4/17.4 °C; Total cooling capacity 22 °C (50/70 %) - 6/12 °C=31.4/44.7 kW; Total cooling capacity 22 °C (50/70 %) - 8/14 °C=31.4/28.2 kW; Total cooling capacity 26 °C (50/70 %) - 6/12 °C=49.9/69.8 kW; Total cooling capacity 26 °C (50/70 %) - 8/14 °C=35.0/53.2 kW; Total sound power level=82 dB(A); Water content of cooling coil=12.4 l; Water content of heating coil=12.4 l; Water pressure drop 16/20 °C (60/40 °C)=6/5 kPa; Water pressure drop 16/20 °C (80/60 °C)=18/15 kPa; Water pressure drop 22 °C (50/70 %) - 6/12 °C=15/31 kPa; Water pressure drop 22 °C (50/70 %) - 8/14 °C=15/12 kPa; Water pressure drop 26 °C (50/70 %) - 6/12 °C=38/75 kPa; Water pressure drop 26 °C (50/70 %) - 8/14 °C=19/44 kPa; Water quantity 16/20 °C (60/40 °C)=3003/2622 l/h; Water quantity 16/20 °C (80/60 °C)=5066/4686 l/h; Water quantity 22 °C (50/70 %) - 6/12 °C=4496/6401 l/h; Water quantity 22 °C (50/70 %) - 8/14 °C=4496/4031 l/h; Water quantity 26 °C (50/70 %) - 6/12 °C=7149/9989 l/h; Water quantity 26 °C (50/70 %) - 8/14 °C=5013/7619 l/h; Weight=329 kg
- THC-9-AD: (X)=1238 mm  [stored 4.06168 ft]; A=1100 mm; Air flow rate=5000 m3/h; B=1765 mm  [stored 5.79068 ft]; COBIE Air flow rate=5000 m3/h; COBIE Condensate quantity=150 kg/h; COBIE Condensate quantity 22 °C (50/70 %) - 6/12 °C=0.0/32.5 kg/h; COBIE Condensate quantity 22 °C (50/70 %) - 8/14 °C=0.0/22.6 kg/h; COBIE Condensate quantity 26 °C (50/70 %) - 6/12 °C=23.5/63.9 kg/h; COBIE Condensate quantity 26 °C (50/70 %) - 8/14 °C=13.6/54.0 kg/h; COBIE Effective electric power input=1.54 kW; COBIE Floor area covered=946.0; COBIE Heat output 16/20 °C (60/40 °C)=31.7/27.4 kW; COBIE Heat output 16/20 °C (80/60 °C)=55.5/51.2 kW; COBIE Maximum mounting height 16/20 °C (60/40 °C)=17.0/18.1 m; COBIE Maximum mounting height 16/20 °C (80/60 °C)=13.6/14.1 m; COBIE Nominal air flow rate=9000.0; COBIE Octave sound power level - 1000 Hz=77 dB; COBIE Octave sound power level - 125 Hz=66 dB; COBIE Octave sound power level - 2000 Hz=76 dB; COBIE Octave sound power level - 250 Hz=69 dB; COBIE Octave sound power level - 4000 Hz=74 dB; COBIE Octave sound power level - 500 Hz=74 dB; COBIE Octave sound power level - 63 Hz=47 dB; COBIE Octave sound power level - 8000 Hz=67 dB; COBIE Sensible cooling capacity 22 °C (50/70 %) - 6/12 °C=37.1/34.6 kW; COBIE Sensible cooling capacity 22 °C (50/70 %) - 8/14 °C=37.1/29.7 kW; COBIE Sensible cooling capacity 26 °C (50/70 %) - 6/12 °C=46.4/43.9 kW; COBIE Sensible cooling capacity 26 °C (50/70 %) - 8/14 °C=41.6/39.1 kW; COBIE Sound pressure level (at a distance of 5 m)=60 dB(A); COBIE Supply air temperature 16/20 °C (60/40 °C)=28.5/31.1 °C; COBIE Supply air temperature 16/20 °C (80/60 °C)=36.3/38.9 °C; COBIE Supply air temperature 22 °C (50/70 %) - 6/12 °C=11.8/12.6 °C; COBIE Supply air temperature 22 °C (50/70 %) - 8/14 °C=11.8/14.2 °C; COBIE Supply air temperature 26 °C (50/70 %) - 6/12 °C=12.7/13.5 °C; COBIE Supply air temperature 26 °C (50/70 %) - 8/14 °C=14.3/15.1 °C; COBIE Total cooling capacity 22 °C (50/70 %) - 6/12 °C=37.1/56.7 kW; COBIE Total cooling capacity 22 °C (50/70 %) - 8/14 °C=37.1/45.1 kW; COBIE Total cooling capacity 26 °C (50/70 %) - 6/12 °C=62.4/87.4 kW; COBIE Total cooling capacity 26 °C (50/70 %) - 8/14 °C=50.9/75.8 kW; COBIE Total sound power level=82 dB(A); COBIE Water content of cooling coil=19.2 l; COBIE Water content of heating coil=7.4 l; COBIE Water pressure drop 16/20 °C (60/40 °C)=3/2 kPa; COBIE Water pressure drop 16/20 °C (80/60 °C)=8/7 kPa; COBIE Water pressure drop 22 °C (50/70 %) - 6/12 °C=13/30 kPa; COBIE Water pressure drop 22 °C (50/70 %) - 8/14 °C=13/19 kPa; COBIE Water pressure drop 26 °C (50/70 %) - 6/12 °C=36/70 kPa; COBIE Water pressure drop 26 °C (50/70 %) - 8/14 °C=24/53 kPa; COBIE Water quantity 16/20 °C (60/40 °C)=1364/1179 l/h; COBIE Water quantity 16/20 °C (80/60 °C)=2386/2201 l/h; COBIE Water quantity 22 °C (50/70 %) - 6/12 °C=5307/8118 l/h; COBIE Water quantity 22 °C (50/70 %) - 8/14 °C=5307/6459 l/h; COBIE Water quantity 26 °C (50/70 %) - 6/12 °C=8941/12513 l/h; COBIE Water quantity 26 °C (50/70 %) - 8/14 °C=7282/10854 l/h; COBIE Weight=329 kg; Condensate quantity=150 kg/h; Condensate quantity 22 °C (50/70 %) - 6/12 °C=0.0/32.5 kg/h; Condensate quantity 22 °C (50/70 %) - 8/14 °C=0.0/22.6 kg/h; Condensate quantity 26 °C (50/70 %) - 6/12 °C=23.5/63.9 kg/h; Condensate quantity 26 °C (50/70 %) - 8/14 °C=13.6/54.0 kg/h; E=846 mm  [stored 2.77559 ft]; E/2=423 mm  [stored 1.3878 ft]; Effective electric power input=1.54 kW; F=882 mm  [stored 2.8937 ft]; Floor area covered=946 m²; G=111 mm; H=189 mm  [stored 0.620079 ft]; Heat output 16/20 °C (60/40 °C)=31.7/27.4 kW; Heat output 16/20 °C (80/60 °C)=55.5/51.2 kW; I=395 mm  [stored 1.29593 ft]; J=473 mm  [stored 1.55184 ft]; K=935 mm; Maximum mounting height 16/20 °C (60/40 °C)=17.0/18.1 m; Maximum mounting height 16/20 °C (80/60 °C)=13.6/14.1 m; N=1230 mm  [stored 4.03543 ft]; Nominal air flow rate=9000 m³/h; O=860 mm; Octave sound power level - 1000 Hz=77 dB; Octave sound power level - 125 Hz=66 dB; Octave sound power level - 2000 Hz=76 dB; Octave sound power level - 250 Hz=69 dB; Octave sound power level - 4000 Hz=74 dB; Octave sound power level - 500 Hz=74 dB; Octave sound power level - 63 Hz=47 dB; Octave sound power level - 8000 Hz=67 dB; P=342 mm  [stored 1.12205 ft]; Q=38 mm; R=51 mm; Sensible cooling capacity 22 °C (50/70 %) - 6/12 °C=37.1/34.6 kW; Sensible cooling capacity 22 °C (50/70 %) - 8/14 °C=37.1/29.7 kW; Sensible cooling capacity 26 °C (50/70 %) - 6/12 °C=46.4/43.9 kW; Sensible cooling capacity 26 °C (50/70 %) - 8/14 °C=41.6/39.1 kW; Sound pressure level (at a distance of 5 m)=60 dB(A); Supply air temperature 16/20 °C (60/40 °C)=28.5/31.1 °C; Supply air temperature 16/20 °C (80/60 °C)=36.3/38.9 °C; Supply air temperature 22 °C (50/70 %) - 6/12 °C=11.8/12.6 °C; Supply air temperature 22 °C (50/70 %) - 8/14 °C=11.8/14.2 °C; Supply air temperature 26 °C (50/70 %) - 6/12 °C=12.7/13.5 °C; Supply air temperature 26 °C (50/70 %) - 8/14 °C=14.3/15.1 °C; Total cooling capacity 22 °C (50/70 %) - 6/12 °C=37.1/56.7 kW; Total cooling capacity 22 °C (50/70 %) - 8/14 °C=37.1/45.1 kW; Total cooling capacity 26 °C (50/70 %) - 6/12 °C=62.4/87.4 kW; Total cooling capacity 26 °C (50/70 %) - 8/14 °C=50.9/75.8 kW; Total sound power level=82 dB(A); Water content of cooling coil=19.2 l; Water content of heating coil=7.4 l; Water pressure drop 16/20 °C (60/40 °C)=3/2 kPa; Water pressure drop 16/20 °C (80/60 °C)=8/7 kPa; Water pressure drop 22 °C (50/70 %) - 6/12 °C=13/30 kPa; Water pressure drop 22 °C (50/70 %) - 8/14 °C=13/19 kPa; Water pressure drop 26 °C (50/70 %) - 6/12 °C=36/70 kPa; Water pressure drop 26 °C (50/70 %) - 8/14 °C=24/53 kPa; Water quantity 16/20 °C (60/40 °C)=1364/1179 l/h; Water quantity 16/20 °C (80/60 °C)=2386/2201 l/h; Water quantity 22 °C (50/70 %) - 6/12 °C=5307/8118 l/h; Water quantity 22 °C (50/70 %) - 8/14 °C=5307/6459 l/h; Water quantity 26 °C (50/70 %) - 6/12 °C=8941/12513 l/h; Water quantity 26 °C (50/70 %) - 8/14 °C=7282/10854 l/h; Weight=329 kg
- THC-9-BD: (X)=1238 mm  [stored 4.06168 ft]; A=1100 mm; Air flow rate=5000 m3/h; B=1765 mm  [stored 5.79068 ft]; COBIE Air flow rate=5000 m3/h; COBIE Condensate quantity=150 kg/h; COBIE Condensate quantity 22 °C (50/70 %) - 6/12 °C=0.0/32.5 kg/h; COBIE Condensate quantity 22 °C (50/70 %) - 8/14 °C=0.0/22.6 kg/h; COBIE Condensate quantity 26 °C (50/70 %) - 6/12 °C=23.5/63.9 kg/h; COBIE Condensate quantity 26 °C (50/70 %) - 8/14 °C=13.6/54.0 kg/h; COBIE Effective electric power input=1.56 kW; COBIE Floor area covered=946.0; COBIE Heat output 16/20 °C (60/40 °C)=40.6/35.1 kW; COBIE Heat output 16/20 °C (80/60 °C)=71.2/65.7 kW; COBIE Maximum mounting height 16/20 °C (60/40 °C)=15.4/16.5 m; COBIE Maximum mounting height 16/20 °C (80/60 °C)=12.2/12.7 m; COBIE Nominal air flow rate=9000.0; COBIE Octave sound power level - 1000 Hz=77 dB; COBIE Octave sound power level - 125 Hz=66 dB; COBIE Octave sound power level - 2000 Hz=76 dB; COBIE Octave sound power level - 250 Hz=69 dB; COBIE Octave sound power level - 4000 Hz=74 dB; COBIE Octave sound power level - 500 Hz=74 dB; COBIE Octave sound power level - 63 Hz=47 dB; COBIE Octave sound power level - 8000 Hz=67 dB; COBIE Sensible cooling capacity 22 °C (50/70 %) - 6/12 °C=37.1/34.6 kW; COBIE Sensible cooling capacity 22 °C (50/70 %) - 8/14 °C=37.1/29.7 kW; COBIE Sensible cooling capacity 26 °C (50/70 %) - 6/12 °C=46.4/43.9 kW; COBIE Sensible cooling capacity 26 °C (50/70 %) - 8/14 °C=41.6/39.1 kW; COBIE Sound pressure level (at a distance of 5 m)=60 dB(A); COBIE Supply air temperature 16/20 °C (60/40 °C)=31.4/33.6 °C; COBIE Supply air temperature 16/20 °C (80/60 °C)=41.5/43.7 °C; COBIE Supply air temperature 22 °C (50/70 %) - 6/12 °C=11.8/12.6 °C; COBIE Supply air temperature 22 °C (50/70 %) - 8/14 °C=11.8/14.2 °C; COBIE Supply air temperature 26 °C (50/70 %) - 6/12 °C=12.7/13.5 °C; COBIE Supply air temperature 26 °C (50/70 %) - 8/14 °C=14.3/15.1 °C; COBIE Total cooling capacity 22 °C (50/70 %) - 6/12 °C=37.1/56.7 kW; COBIE Total cooling capacity 22 °C (50/70 %) - 8/14 °C=37.1/45.1 kW; COBIE Total cooling capacity 26 °C (50/70 %) - 6/12 °C=62.4/87.4 kW; COBIE Total cooling capacity 26 °C (50/70 %) - 8/14 °C=50.9/75.8 kW; COBIE Total sound power level=82 dB(A); COBIE Water content of cooling coil=19.2 l; COBIE Water content of heating coil=7.4 l; COBIE Water pressure drop 16/20 °C (60/40 °C)=4/3 kPa; COBIE Water pressure drop 16/20 °C (80/60 °C)=12/10 kPa; COBIE Water pressure drop 22 °C (50/70 %) - 6/12 °C=13/30 kPa; COBIE Water pressure drop 22 °C (50/70 %) - 8/14 °C=13/19 kPa; COBIE Water pressure drop 26 °C (50/70 %) - 6/12 °C=36/70 kPa; COBIE Water pressure drop 26 °C (50/70 %) - 8/14 °C=24/53 kPa; COBIE Water quantity 16/20 °C (60/40 °C)=1746/1509 l/h; COBIE Water quantity 16/20 °C (80/60 °C)=3060/2823 l/h; COBIE Water quantity 22 °C (50/70 %) - 6/12 °C=5307/8118 l/h; COBIE Water quantity 22 °C (50/70 %) - 8/14 °C=5307/6459 l/h; COBIE Water quantity 26 °C (50/70 %) - 6/12 °C=8941/12513 l/h; COBIE Water quantity 26 °C (50/70 %) - 8/14 °C=7282/10854 l/h; COBIE Weight=329 kg; Condensate quantity=150 kg/h; Condensate quantity 22 °C (50/70 %) - 6/12 °C=0.0/32.5 kg/h; Condensate quantity 22 °C (50/70 %) - 8/14 °C=0.0/22.6 kg/h; Condensate quantity 26 °C (50/70 %) - 6/12 °C=23.5/63.9 kg/h; Condensate quantity 26 °C (50/70 %) - 8/14 °C=13.6/54.0 kg/h; E=846 mm  [stored 2.77559 ft]; E/2=423 mm  [stored 1.3878 ft]; Effective electric power input=1.56 kW; F=882 mm  [stored 2.8937 ft]; Floor area covered=946 m²; G=111 mm; H=189 mm  [stored 0.620079 ft]; Heat output 16/20 °C (60/40 °C)=40.6/35.1 kW; Heat output 16/20 °C (80/60 °C)=71.2/65.7 kW; I=395 mm  [stored 1.29593 ft]; J=473 mm  [stored 1.55184 ft]; K=935 mm; Maximum mounting height 16/20 °C (60/40 °C)=15.4/16.5 m; Maximum mounting height 16/20 °C (80/60 °C)=12.2/12.7 m; N=1230 mm  [stored 4.03543 ft]; Nominal air flow rate=9000 m³/h; O=860 mm; Octave sound power level - 1000 Hz=77 dB; Octave sound power level - 125 Hz=66 dB; Octave sound power level - 2000 Hz=76 dB; Octave sound power level - 250 Hz=69 dB; Octave sound power level - 4000 Hz=74 dB; Octave sound power level - 500 Hz=74 dB; Octave sound power level - 63 Hz=47 dB; Octave sound power level - 8000 Hz=67 dB; P=342 mm  [stored 1.12205 ft]; Q=38 mm; R=51 mm; Sensible cooling capacity 22 °C (50/70 %) - 6/12 °C=37.1/34.6 kW; Sensible cooling capacity 22 °C (50/70 %) - 8/14 °C=37.1/29.7 kW; Sensible cooling capacity 26 °C (50/70 %) - 6/12 °C=46.4/43.9 kW; Sensible cooling capacity 26 °C (50/70 %) - 8/14 °C=41.6/39.1 kW; Sound pressure level (at a distance of 5 m)=60 dB(A); Supply air temperature 16/20 °C (60/40 °C)=31.4/33.6 °C; Supply air temperature 16/20 °C (80/60 °C)=41.5/43.7 °C; Supply air temperature 22 °C (50/70 %) - 6/12 °C=11.8/12.6 °C; Supply air temperature 22 °C (50/70 %) - 8/14 °C=11.8/14.2 °C; Supply air temperature 26 °C (50/70 %) - 6/12 °C=12.7/13.5 °C; Supply air temperature 26 °C (50/70 %) - 8/14 °C=14.3/15.1 °C; Total cooling capacity 22 °C (50/70 %) - 6/12 °C=37.1/56.7 kW; Total cooling capacity 22 °C (50/70 %) - 8/14 °C=37.1/45.1 kW; Total cooling capacity 26 °C (50/70 %) - 6/12 °C=62.4/87.4 kW; Total cooling capacity 26 °C (50/70 %) - 8/14 °C=50.9/75.8 kW; Total sound power level=82 dB(A); Water content of cooling coil=19.2 l; Water content of heating coil=7.4 l; Water pressure drop 16/20 °C (60/40 °C)=4/3 kPa; Water pressure drop 16/20 °C (80/60 °C)=12/10 kPa; Water pressure drop 22 °C (50/70 %) - 6/12 °C=13/30 kPa; Water pressure drop 22 °C (50/70 %) - 8/14 °C=13/19 kPa; Water pressure drop 26 °C (50/70 %) - 6/12 °C=36/70 kPa; Water pressure drop 26 °C (50/70 %) - 8/14 °C=24/53 kPa; Water quantity 16/20 °C (60/40 °C)=1746/1509 l/h; Water quantity 16/20 °C (80/60 °C)=3060/2823 l/h; Water quantity 22 °C (50/70 %) - 6/12 °C=5307/8118 l/h; Water quantity 22 °C (50/70 %) - 8/14 °C=5307/6459 l/h; Water quantity 26 °C (50/70 %) - 6/12 °C=8941/12513 l/h; Water quantity 26 °C (50/70 %) - 8/14 °C=7282/10854 l/h; Weight=329 kg
- THC-9-CD: (X)=1238 mm  [stored 4.06168 ft]; A=1100 mm; Air flow rate=5000 m3/h; B=1765 mm  [stored 5.79068 ft]; COBIE Air flow rate=5000 m3/h; COBIE Condensate quantity=150 kg/h; COBIE Condensate quantity 22 °C (50/70 %) - 6/12 °C=0.0/32.5 kg/h; COBIE Condensate quantity 22 °C (50/70 %) - 8/14 °C=0.0/22.6 kg/h; COBIE Condensate quantity 26 °C (50/70 %) - 6/12 °C=23.5/63.9 kg/h; COBIE Condensate quantity 26 °C (50/70 %) - 8/14 °C=13.6/54.0 kg/h; COBIE Effective electric power input=1.68 kW; COBIE Floor area covered=946.0; COBIE Heat output 16/20 °C (60/40 °C)=69.9/61.0 kW; COBIE Heat output 16/20 °C (80/60 °C)=117.9/109.1 kW; COBIE Maximum mounting height 16/20 °C (60/40 °C)=12.3/13.1 m; COBIE Maximum mounting height 16/20 °C (80/60 °C)=9.8/10.2 m; COBIE Nominal air flow rate=9000.0; COBIE Octave sound power level - 1000 Hz=77 dB; COBIE Octave sound power level - 125 Hz=66 dB; COBIE Octave sound power level - 2000 Hz=76 dB; COBIE Octave sound power level - 250 Hz=69 dB; COBIE Octave sound power level - 4000 Hz=74 dB; COBIE Octave sound power level - 500 Hz=74 dB; COBIE Octave sound power level - 63 Hz=47 dB; COBIE Octave sound power level - 8000 Hz=67 dB; COBIE Sensible cooling capacity 22 °C (50/70 %) - 6/12 °C=37.1/34.6 kW; COBIE Sensible cooling capacity 22 °C (50/70 %) - 8/14 °C=37.1/29.7 kW; COBIE Sensible cooling capacity 26 °C (50/70 %) - 6/12 °C=46.4/43.9 kW; COBIE Sensible cooling capacity 26 °C (50/70 %) - 8/14 °C=41.6/39.1 kW; COBIE Sound pressure level (at a distance of 5 m)=60 dB(A); COBIE Supply air temperature 16/20 °C (60/40 °C)=41.1/42.1 °C; COBIE Supply air temperature 16/20 °C (80/60 °C)=56.9/58.0 °C; COBIE Supply air temperature 22 °C (50/70 %) - 6/12 °C=11.8/12.6 °C; COBIE Supply air temperature 22 °C (50/70 %) - 8/14 °C=11.8/14.2 °C; COBIE Supply air temperature 26 °C (50/70 %) - 6/12 °C=12.7/13.5 °C; COBIE Supply air temperature 26 °C (50/70 %) - 8/14 °C=14.3/15.1 °C; COBIE Total cooling capacity 22 °C (50/70 %) - 6/12 °C=37.1/56.7 kW; COBIE Total cooling capacity 22 °C (50/70 %) - 8/14 °C=37.1/45.1 kW; COBIE Total cooling capacity 26 °C (50/70 %) - 6/12 °C=62.4/87.4 kW; COBIE Total cooling capacity 26 °C (50/70 %) - 8/14 °C=50.9/75.8 kW; COBIE Total sound power level=82 dB(A); COBIE Water content of cooling coil=19.2 l; COBIE Water content of heating coil=12.4 l; COBIE Water pressure drop 16/20 °C (60/40 °C)=6/5 kPa; COBIE Water pressure drop 16/20 °C (80/60 °C)=18/15 kPa; COBIE Water pressure drop 22 °C (50/70 %) - 6/12 °C=13/30 kPa; COBIE Water pressure drop 22 °C (50/70 %) - 8/14 °C=13/19 kPa; COBIE Water pressure drop 26 °C (50/70 %) - 6/12 °C=36/70 kPa; COBIE Water pressure drop 26 °C (50/70 %) - 8/14 °C=24/53 kPa; COBIE Water quantity 16/20 °C (60/40 °C)=3003/2622 l/h; COBIE Water quantity 16/20 °C (80/60 °C)=5066/4686 l/h; COBIE Water quantity 22 °C (50/70 %) - 6/12 °C=5307/8118 l/h; COBIE Water quantity 22 °C (50/70 %) - 8/14 °C=5307/6459 l/h; COBIE Water quantity 26 °C (50/70 %) - 6/12 °C=8941/12513 l/h; COBIE Water quantity 26 °C (50/70 %) - 8/14 °C=7282/10854 l/h; COBIE Weight=340 kg; Condensate quantity=150 kg/h; Condensate quantity 22 °C (50/70 %) - 6/12 °C=0.0/32.5 kg/h; Condensate quantity 22 °C (50/70 %) - 8/14 °C=0.0/22.6 kg/h; Condensate quantity 26 °C (50/70 %) - 6/12 °C=23.5/63.9 kg/h; Condensate quantity 26 °C (50/70 %) - 8/14 °C=13.6/54.0 kg/h; E=846 mm  [stored 2.77559 ft]; E/2=423 mm  [stored 1.3878 ft]; Effective electric power input=1.68 kW; F=882 mm  [stored 2.8937 ft]; Floor area covered=946 m²; G=111 mm; H=189 mm  [stored 0.620079 ft]; Heat output 16/20 °C (60/40 °C)=69.9/61.0 kW; Heat output 16/20 °C (80/60 °C)=117.9/109.1 kW; I=395 mm  [stored 1.29593 ft]; J=473 mm  [stored 1.55184 ft]; K=935 mm; Maximum mounting height 16/20 °C (60/40 °C)=12.3/13.1 m; Maximum mounting height 16/20 °C (80/60 °C)=9.8/10.2 m; N=1230 mm  [stored 4.03543 ft]; Nominal air flow rate=9000 m³/h; O=860 mm; Octave sound power level - 1000 Hz=77 dB; Octave sound power level - 125 Hz=66 dB; Octave sound power level - 2000 Hz=76 dB; Octave sound power level - 250 Hz=69 dB; Octave sound power level - 4000 Hz=74 dB; Octave sound power level - 500 Hz=74 dB; Octave sound power level - 63 Hz=47 dB; Octave sound power level - 8000 Hz=67 dB; P=342 mm  [stored 1.12205 ft]; Q=38 mm; R=51 mm; Sensible cooling capacity 22 °C (50/70 %) - 6/12 °C=37.1/34.6 kW; Sensible cooling capacity 22 °C (50/70 %) - 8/14 °C=37.1/29.7 kW; Sensible cooling capacity 26 °C (50/70 %) - 6/12 °C=46.4/43.9 kW; Sensible cooling capacity 26 °C (50/70 %) - 8/14 °C=41.6/39.1 kW; Sound pressure level (at a distance of 5 m)=60 dB(A); Supply air temperature 16/20 °C (60/40 °C)=41.1/42.1 °C; Supply air temperature 16/20 °C (80/60 °C)=56.9/58.0 °C; Supply air temperature 22 °C (50/70 %) - 6/12 °C=11.8/12.6 °C; Supply air temperature 22 °C (50/70 %) - 8/14 °C=11.8/14.2 °C; Supply air temperature 26 °C (50/70 %) - 6/12 °C=12.7/13.5 °C; Supply air temperature 26 °C (50/70 %) - 8/14 °C=14.3/15.1 °C; Total cooling capacity 22 °C (50/70 %) - 6/12 °C=37.1/56.7 kW; Total cooling capacity 22 °C (50/70 %) - 8/14 °C=37.1/45.1 kW; Total cooling capacity 26 °C (50/70 %) - 6/12 °C=62.4/87.4 kW; Total cooling capacity 26 °C (50/70 %) - 8/14 °C=50.9/75.8 kW; Total sound power level=82 dB(A); Water content of cooling coil=19.2 l; Water content of heating coil=12.4 l; Water pressure drop 16/20 °C (60/40 °C)=6/5 kPa; Water pressure drop 16/20 °C (80/60 °C)=18/15 kPa; Water pressure drop 22 °C (50/70 %) - 6/12 °C=13/30 kPa; Water pressure drop 22 °C (50/70 %) - 8/14 °C=13/19 kPa; Water pressure drop 26 °C (50/70 %) - 6/12 °C=36/70 kPa; Water pressure drop 26 °C (50/70 %) - 8/14 °C=24/53 kPa; Water quantity 16/20 °C (60/40 °C)=3003/2622 l/h; Water quantity 16/20 °C (80/60 °C)=5066/4686 l/h; Water quantity 22 °C (50/70 %) - 6/12 °C=5307/8118 l/h; Water quantity 22 °C (50/70 %) - 8/14 °C=5307/6459 l/h; Water quantity 26 °C (50/70 %) - 6/12 °C=8941/12513 l/h; Water quantity 26 °C (50/70 %) - 8/14 °C=7282/10854 l/h; Weight=340 kg

note: [stored X ft] marks values corroborated as IEEE doubles in the binary element streams (Revit-internal decimal feet)

## geometry (parser evidence)
native form markers: Sweep x7
no freeform markers — native parametric forms only
